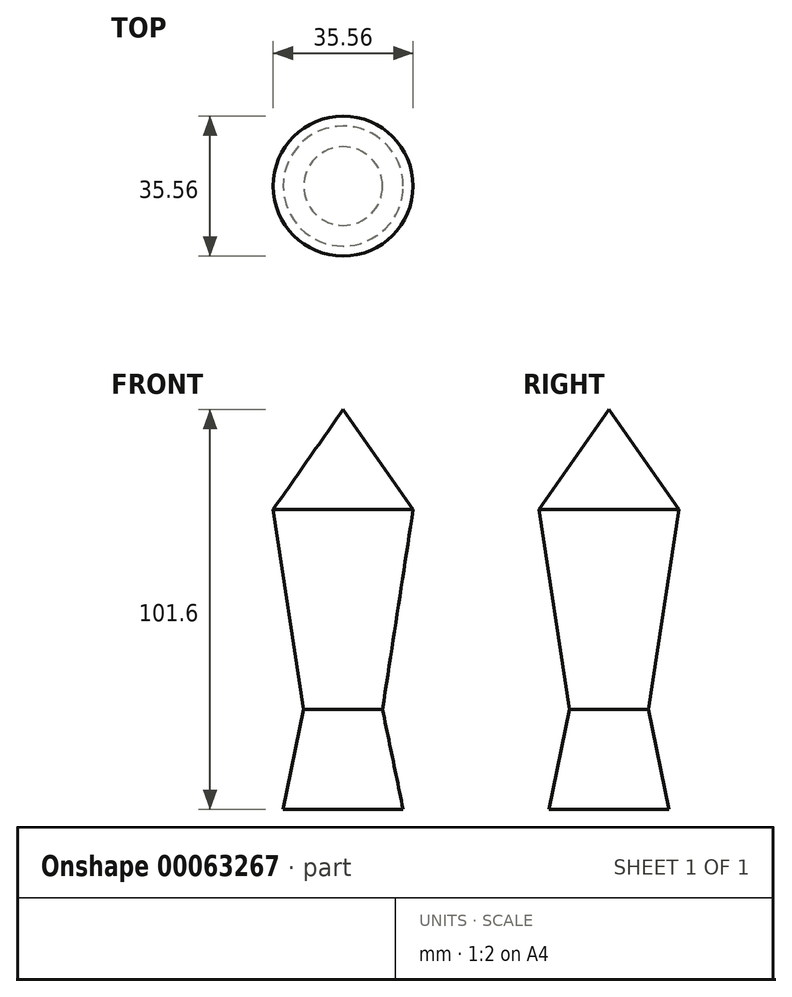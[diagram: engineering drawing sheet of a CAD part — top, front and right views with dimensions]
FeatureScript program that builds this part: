
annotation { "Feature Type Name" : "Feature", "Feature Type Description" : "" }
export const myFeature = defineFeature(function(context is Context, id is Id, definition is map)
    precondition{}
    {
        {
            var Q0;
            Q0=qCreatedBy(makeId("Front.planeOp"),FACE);
            var sketch = newSketch(context, id + "F0", { "sketchPlane" : qUnion([Q0])});
            skLineSegment(sketch, "E0", {"start": v(0, 0) * mm, "end": v(-15.24, 0) * mm});
            skLineSegment(sketch, "E1", {"start": v(0, 25.4) * mm, "end": v(0, 0) * mm});
            skLineSegment(sketch, "E2", {"start": v(-15.24, 0) * mm, "end": v(-10, 25.4) * mm});
            skLineSegment(sketch, "E3", {"start": v(-10, 25.4) * mm, "end": v(0, 25.4) * mm});
            skSolve(sketch);
        }
        {
            var Q0;
            Q0 = qSketchRegion(id + "F0", true);
            var Q1;
            Q1=sQuery(id+"F0.wireOp",EDGE,"E1");
            revolve(context, id + "F1", {"entities" : qUnion([Q0]), "axis" : qUnion([Q1]), "revolveType" : RevolveType.FULL});
        }
        {
            var Q0;
            Q0=qCreatedBy(makeId("Front.planeOp"),FACE);
            var sketch = newSketch(context, id + "F2", { "sketchPlane" : qUnion([Q0])});
            skLineSegment(sketch, "E4", {"start": v(-15.34, -0.5) * mm, "end": v(-10, 25.4) * mm});
            skLineSegment(sketch, "E5", {"start": v(10, 25.4) * mm, "end": v(15.34, -0.5) * mm});
            skLineSegment(sketch, "E6", {"start": v(-10, 25.4) * mm, "end": v(10, 25.4) * mm});
            skLineSegment(sketch, "E7", {"start": v(0, 25.4) * mm, "end": v(0, 76.2) * mm});
            skPoint(sketch, "E7.endSnap0", {"position": v(0, 25.4) * mm});
            skLineSegment(sketch, "E8", {"start": v(0, 76.2) * mm, "end": v(-17.78, 76.2) * mm});
            skLineSegment(sketch, "E9", {"start": v(-17.78, 76.2) * mm, "end": v(-10, 25.4) * mm});
            skSolve(sketch);
        }
        {
            var Q0;
            {var subQ2=sQuery(id+"F2.wireOp",EDGE,"E7");Q0=makeQuery(id+"F2.imprint","IMPRINT",FACE,{"disambiguationData":[TD([[makeQuery(id+"F2.imprint","IMPRINT",EDGE,{"derivedFrom":subQ2}),1.0]])]});}
            var Q1;
            Q1=sQuery(id+"F2.wireOp",EDGE,"E7");
            revolve(context, id + "F3", {"operationType" : NewBodyOperationType.ADD, "entities" : qUnion([Q0]), "axis" : qUnion([Q1]), "revolveType" : RevolveType.FULL});
        }
        {
            var Q0;
            Q0=qCreatedBy(makeId("Front.planeOp"),FACE);
            var sketch = newSketch(context, id + "F4", { "sketchPlane" : qUnion([Q0])});
            skLineSegment(sketch, "E10", {"start": v(17.78, 76.2) * mm, "end": v(10, 25.4) * mm});
            skLineSegment(sketch, "E11", {"start": v(-10, 25.4) * mm, "end": v(-17.78, 76.2) * mm});
            skLineSegment(sketch, "E12", {"start": v(-17.78, 76.2) * mm, "end": v(17.78, 76.2) * mm});
            skLineSegment(sketch, "E13", {"start": v(0, 76.2) * mm, "end": v(0, 101.6) * mm});
            skPoint(sketch, "E13.endSnap0", {"position": v(0, 76.2) * mm});
            skLineSegment(sketch, "E14", {"start": v(0, 101.6) * mm, "end": v(-17.78, 76.2) * mm});
            skSolve(sketch);
        }
        {
            var Q0;
            {var subQ2=sQuery(id+"F4.wireOp",EDGE,"E13");Q0=makeQuery(id+"F4.imprint","IMPRINT",FACE,{"disambiguationData":[TD([[makeQuery(id+"F4.imprint","IMPRINT",EDGE,{"derivedFrom":subQ2}),1.0]])]});}
            var Q1;
            Q1=sQuery(id+"F4.wireOp",EDGE,"E13");
            revolve(context, id + "F5", {"operationType" : NewBodyOperationType.ADD, "entities" : qUnion([Q0]), "axis" : qUnion([Q1]), "revolveType" : RevolveType.FULL});
        }
    });
